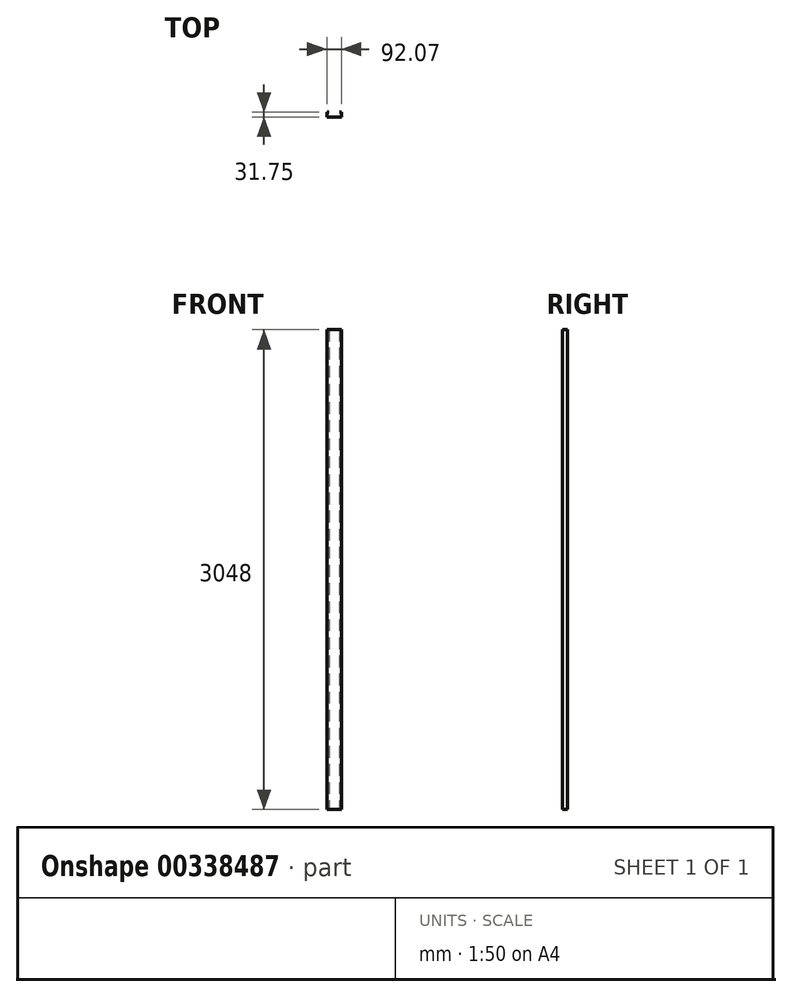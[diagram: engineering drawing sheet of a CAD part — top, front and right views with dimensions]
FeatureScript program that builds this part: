
annotation { "Feature Type Name" : "Feature", "Feature Type Description" : "" }
export const myFeature = defineFeature(function(context is Context, id is Id, definition is map)
    precondition{}
    {
        {
            var Q0;
            Q0=qCreatedBy(makeId("Top.planeOp"),FACE);
            var sketch = newSketch(context, id + "F0", { "sketchPlane" : qUnion([Q0])});
            skLineSegment(sketch, "E0", {"start": v(-91.26, 0) * mm, "end": v(-0.1, 0) * mm});
            skLineSegment(sketch, "E1", {"start": v(-0.1, 0) * mm, "end": v(-0.1, 30.84) * mm});
            skLineSegment(sketch, "E2", {"start": v(-0.1, 30.84) * mm, "end": v(-12.34, 30.84) * mm});
            skLineSegment(sketch, "E3", {"start": v(-91.26, 0) * mm, "end": v(-91.26, 30.84) * mm});
            skLineSegment(sketch, "E4", {"start": v(-91.26, 30.84) * mm, "end": v(-79.01, 30.84) * mm});
            skLineSegment(sketch, "E5.0", {"start": v(-91.71, 31.3) * mm, "end": v(-79.01, 31.3) * mm});
            skLineSegment(sketch, "E5.1", {"start": v(0.36, 31.3) * mm, "end": v(-12.34, 31.3) * mm});
            skLineSegment(sketch, "E5.2", {"start": v(0.36, -0.45) * mm, "end": v(0.36, 31.3) * mm});
            skLineSegment(sketch, "E5.3", {"start": v(-91.71, -0.45) * mm, "end": v(0.36, -0.45) * mm});
            skLineSegment(sketch, "E5.4", {"start": v(-91.71, -0.45) * mm, "end": v(-91.71, 31.3) * mm});
            skLineSegment(sketch, "E6", {"start": v(-79.01, 30.84) * mm, "end": v(-79.01, 31.3) * mm});
            skLineSegment(sketch, "E7", {"start": v(-12.34, 30.84) * mm, "end": v(-12.34, 31.3) * mm});
            skSolve(sketch);
        }
        {
            var Q0;
            Q0=makeQuery(id+"F0.imprint","IMPRINT",FACE,{"disambiguationData":[TD([[makeQuery(id+"F0.imprint","IMPRINT",EDGE,{"derivedFrom":sQuery(id+"F0.wireOp",EDGE,"E0")}),-1.0]])]});
            extrude(context, id + "F1", {"entities" : qUnion([Q0]), "depth" : 3048 * mm});
        }
    });
